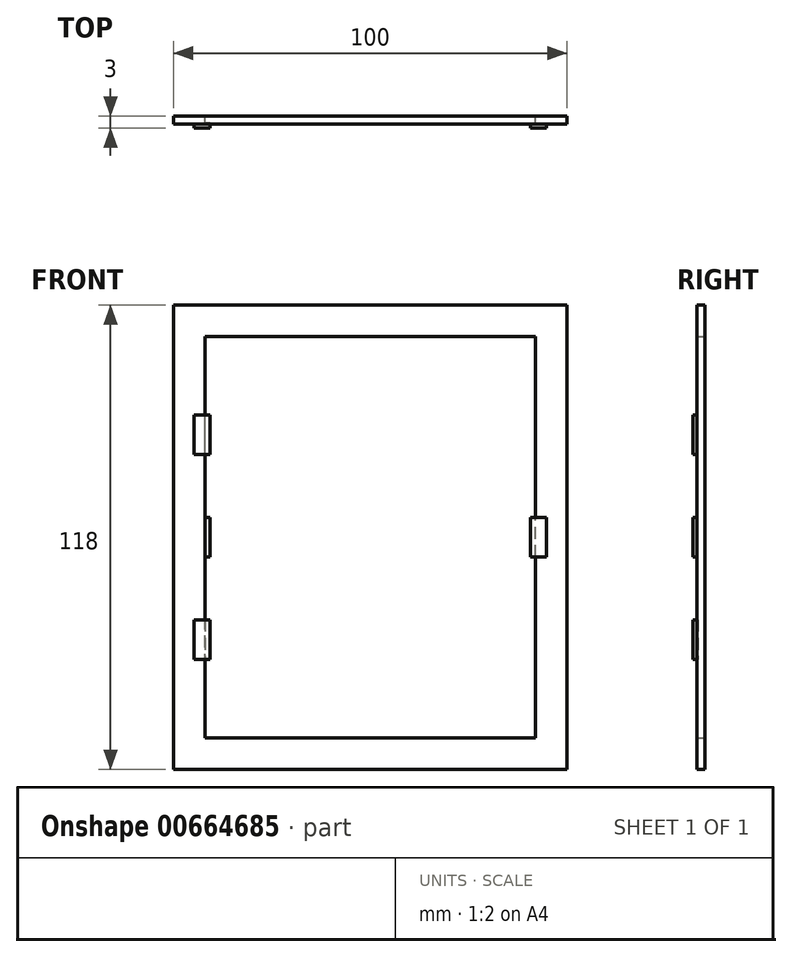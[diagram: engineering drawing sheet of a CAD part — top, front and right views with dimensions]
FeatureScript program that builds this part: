
annotation { "Feature Type Name" : "Feature", "Feature Type Description" : "" }
export const myFeature = defineFeature(function(context is Context, id is Id, definition is map)
    precondition{}
    {
        {
            var Q0;
            Q0=qCreatedBy(makeId("Front.planeOp"),FACE);
            var sketch = newSketch(context, id + "F0", { "sketchPlane" : qUnion([Q0])});
            skLineSegment(sketch, "E0.bottom", {"start": v(0, 0) * mm, "end": v(100, 0) * mm});
            skLineSegment(sketch, "E0.top", {"start": v(0, 118) * mm, "end": v(100, 118) * mm});
            skLineSegment(sketch, "E0.left", {"start": v(0, 0) * mm, "end": v(0, 118) * mm});
            skLineSegment(sketch, "E0.right", {"start": v(100, 0) * mm, "end": v(100, 118) * mm});
            skLineSegment(sketch, "E1.0", {"start": v(92, 8) * mm, "end": v(92, 110) * mm});
            skLineSegment(sketch, "E1.1", {"start": v(8, 8) * mm, "end": v(92, 8) * mm});
            skLineSegment(sketch, "E1.2", {"start": v(8, 8) * mm, "end": v(8, 110) * mm});
            skLineSegment(sketch, "E1.3", {"start": v(8, 110) * mm, "end": v(92, 110) * mm});
            skSolve(sketch);
        }
        {
            var Q0;
            Q0=makeQuery(id+"F0.imprint","IMPRINT",FACE,{"disambiguationData":[TD([[makeQuery(id+"F0.imprint","IMPRINT",EDGE,{"derivedFrom":sQuery(id+"F0.wireOp",EDGE,"E0.bottom")}),1.0]])]});
            extrude(context, id + "F1", {"entities" : qUnion([Q0]), "depth" : 1 * mm, "offsetDistance" : 25 * mm, "hasSecondDirection" : true, "secondDirectionOppositeDirection" : true, "secondDirectionDepth" : 1 * mm});
        }
        {
            var Q0;
            Q0=makeQuery(id+"F1.opExtrude","SWEPT_FACE",FACE,{"disambiguationData":[OSD([sQuery(id+"F0.wireOp",EDGE,"E1.2")])]});
            var sketch = newSketch(context, id + "F2", { "sketchPlane" : qUnion([Q0])});
            skLineSegment(sketch, "E2.bottom", {"start": v(-1, 80) * mm, "end": v(-0.8, 80) * mm});
            skLineSegment(sketch, "E2.top", {"start": v(-1, 90) * mm, "end": v(-0.8, 90) * mm});
            skLineSegment(sketch, "E2.left", {"start": v(-1, 80) * mm, "end": v(-1, 90) * mm});
            skLineSegment(sketch, "E2.right", {"start": v(-0.8, 80) * mm, "end": v(-0.8, 90) * mm});
            skLineSegment(sketch, "E3", {"start": v(-1, 110) * mm, "end": v(-1, 90) * mm});
            skLineSegment(sketch, "E4", {"start": v(-1, 8) * mm, "end": v(-1, 28) * mm});
            skLineSegment(sketch, "E5.bottom", {"start": v(-1, 28) * mm, "end": v(-0.8, 28) * mm});
            skLineSegment(sketch, "E5.top", {"start": v(-1, 38) * mm, "end": v(-0.8, 38) * mm});
            skLineSegment(sketch, "E5.left", {"start": v(-1, 38) * mm, "end": v(-1, 28) * mm});
            skLineSegment(sketch, "E5.right", {"start": v(-0.8, 38) * mm, "end": v(-0.8, 28) * mm});
            skLineSegment(sketch, "E6.bottom", {"start": v(1, 64) * mm, "end": v(0.8, 64) * mm});
            skLineSegment(sketch, "E6.top", {"start": v(1, 54) * mm, "end": v(0.8, 54) * mm});
            skLineSegment(sketch, "E6.left", {"start": v(1, 64) * mm, "end": v(1, 54) * mm});
            skLineSegment(sketch, "E6.right", {"start": v(0.8, 64) * mm, "end": v(0.8, 54) * mm});
            skLineSegment(sketch, "E7", {"start": v(1, 54) * mm, "end": v(1, 8) * mm});
            skLineSegment(sketch, "E8", {"start": v(1, 64) * mm, "end": v(1, 110) * mm});
            skSolve(sketch);
        }
        {
            var Q0;
            Q0 = qSketchRegion(id + "F2", true);
            extrude(context, id + "F3", {"entities" : qUnion([Q0]), "operationType" : NewBodyOperationType.ADD, "depth" : 1.25 * mm, "offsetDistance" : 25 * mm});
        }
        {
            var Q0;
            Q0=qCreatedBy(makeId("Right.planeOp"),FACE);
            cPlane(context, id + "F4", {"entities" : qUnion([Q0]), "cplaneType" : CPlaneType.OFFSET, "offset" : 50 * mm, "width" : 150 * mm, "height" : 150 * mm});
        }
        {
            var Q0;
            Q0=qCreatedBy(id+"F4.planeOp",FACE);
            var sketch = newSketch(context, id + "F5", { "sketchPlane" : qUnion([Q0])});
            skLineSegment(sketch, "E9", {"start": v(0, 0) * mm, "end": v(0, 6.78) * mm});
            skSolve(sketch);
        }
        {
            var Q0;
            Q0=makeQuery(id+"FsCPvsqoQfVQkIM_1.1.F3.boolean.opBoolean","MERGE",FACE,{"derivedFrom":[makeQuery(id+"F3.boolean.opBoolean","MERGE",FACE,{"derivedFrom":[makeQuery(id+"F1.opExtrude","CAP_FACE",FACE,{"disambiguationData":[OSD([sQuery(id+"F0.wireOp",EDGE,"E0.bottom"),sQuery(id+"F0.wireOp",EDGE,"E0.top"),sQuery(id+"F0.wireOp",EDGE,"E0.left"),sQuery(id+"F0.wireOp",EDGE,"E0.right"),sQuery(id+"F0.wireOp",EDGE,"E1.0"),sQuery(id+"F0.wireOp",EDGE,"E1.1"),sQuery(id+"F0.wireOp",EDGE,"E1.2"),sQuery(id+"F0.wireOp",EDGE,"E1.3")])],"isStart":false}),makeQuery(id+"F3.opExtrude","SWEPT_FACE",FACE,{"disambiguationData":[OSD([sQuery(id+"F2.wireOp",EDGE,"E2.left")])]}),makeQuery(id+"F3.opExtrude","SWEPT_FACE",FACE,{"disambiguationData":[OSD([sQuery(id+"F2.wireOp",EDGE,"E5.left")])]})]}),makeQuery(id+"FsCPvsqoQfVQkIM_1.1.F3.opExtrude","SWEPT_FACE",FACE,{"disambiguationData":[OSD([sQuery(id+"F2.wireOp",EDGE,"E6.left")])]})]});
            var sketch = newSketch(context, id + "F6", { "sketchPlane" : qUnion([Q0])});
            skLineSegment(sketch, "E10.bottom", {"start": v(9.25, 38) * mm, "end": v(5.25, 38) * mm});
            skLineSegment(sketch, "E10.top", {"start": v(9.25, 28) * mm, "end": v(5.25, 28) * mm});
            skLineSegment(sketch, "E10.left", {"start": v(9.25, 38) * mm, "end": v(9.25, 28) * mm});
            skLineSegment(sketch, "E10.right", {"start": v(5.25, 38) * mm, "end": v(5.25, 28) * mm});
            skLineSegment(sketch, "E11.bottom", {"start": v(9.25, 80) * mm, "end": v(5.25, 80) * mm});
            skLineSegment(sketch, "E11.top", {"start": v(9.25, 90) * mm, "end": v(5.25, 90) * mm});
            skLineSegment(sketch, "E11.left", {"start": v(9.25, 80) * mm, "end": v(9.25, 90) * mm});
            skLineSegment(sketch, "E11.right", {"start": v(5.25, 80) * mm, "end": v(5.25, 90) * mm});
            skLineSegment(sketch, "E12.bottom", {"start": v(90.75, 54) * mm, "end": v(94.75, 54) * mm});
            skLineSegment(sketch, "E12.top", {"start": v(90.75, 64) * mm, "end": v(94.75, 64) * mm});
            skLineSegment(sketch, "E12.left", {"start": v(90.75, 54) * mm, "end": v(90.75, 64) * mm});
            skLineSegment(sketch, "E12.right", {"start": v(94.75, 54) * mm, "end": v(94.75, 64) * mm});
            skSolve(sketch);
        }
        {
            var Q0;
            Q0 = qSketchRegion(id + "F6", true);
            extrude(context, id + "F7", {"entities" : qUnion([Q0]), "operationType" : NewBodyOperationType.ADD, "depth" : 1 * mm, "offsetDistance" : 25 * mm});
        }
    });
